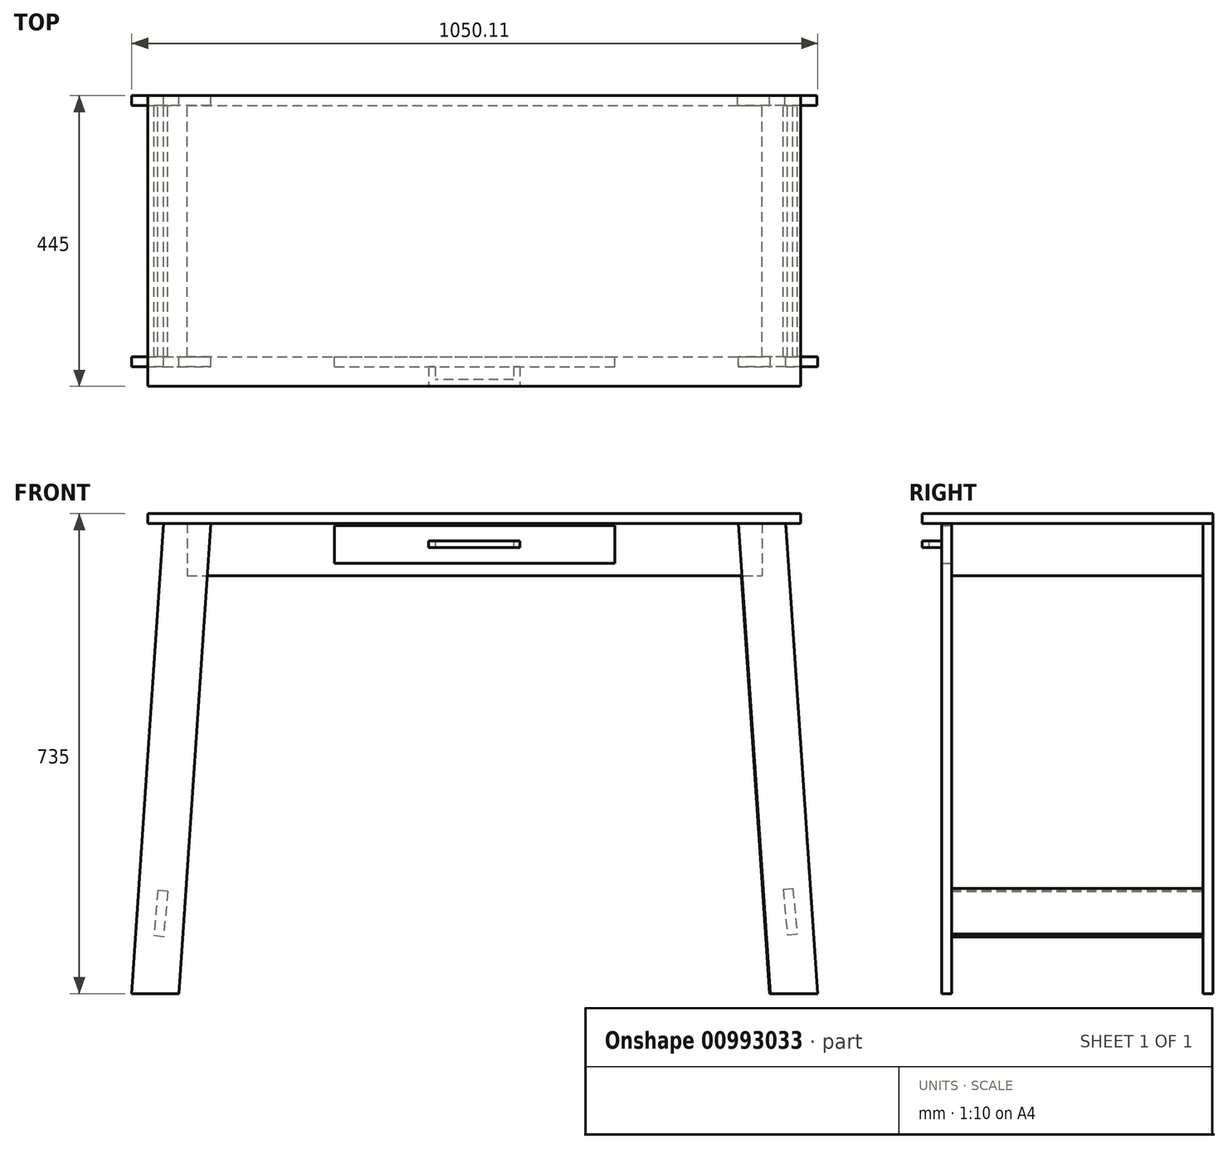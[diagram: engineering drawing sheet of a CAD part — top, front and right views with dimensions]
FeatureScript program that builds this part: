
annotation { "Feature Type Name" : "Feature", "Feature Type Description" : "" }
export const myFeature = defineFeature(function(context is Context, id is Id, definition is map)
    precondition{}
    {
        {
            var Q0;
            Q0=qCreatedBy(makeId("Front.planeOp"),FACE);
            var sketch = newSketch(context, id + "F0", { "sketchPlane" : qUnion([Q0])});
            skLineSegment(sketch, "E0.bottom", {"start": v(500, 7.5) * mm, "end": v(-500, 7.5) * mm});
            skLineSegment(sketch, "E0.top", {"start": v(500, -7.5) * mm, "end": v(-500, -7.5) * mm});
            skLineSegment(sketch, "E0.left", {"start": v(500, 7.5) * mm, "end": v(500, -7.5) * mm});
            skLineSegment(sketch, "E0.right", {"start": v(-500, 7.5) * mm, "end": v(-500, -7.5) * mm});
            skPoint(sketch, "E0.middle", {"position": v(0, 0) * mm});
            skLineSegment(sketch, "E1", {"start": v(-500, -7.5) * mm, "end": v(-475.48, -7.5) * mm});
            skLineSegment(sketch, "E2.bottom", {"start": v(-475.48, -7.5) * mm, "end": v(-403.32, -7.5) * mm});
            skLineSegment(sketch, "E2.left", {"start": v(-475.48, -7.5) * mm, "end": v(-524.46, -727.5) * mm});
            skLineSegment(sketch, "E2.right", {"start": v(-403.32, -7.5) * mm, "end": v(-452.29, -727.5) * mm});
            skLineSegment(sketch, "E3", {"start": v(-524.46, -727.5) * mm, "end": v(-452.29, -727.5) * mm});
            skLineSegment(sketch, "E4.MirrorCS", {"start": v(500, -7.5) * mm, "end": v(475.48, -7.5) * mm});
            skLineSegment(sketch, "E5.MirrorCS", {"start": v(475.48, -7.5) * mm, "end": v(403.32, -7.5) * mm});
            skLineSegment(sketch, "E6.MirrorCS", {"start": v(524.46, -727.5) * mm, "end": v(452.29, -727.5) * mm});
            skLineSegment(sketch, "E7.MirrorCS", {"start": v(475.48, -7.5) * mm, "end": v(524.46, -727.5) * mm});
            skLineSegment(sketch, "E8.MirrorCS", {"start": v(403.32, -7.5) * mm, "end": v(452.29, -727.5) * mm});
            skSolve(sketch);
        }
        {
            var Q0;
            Q0=makeQuery(id+"F0.imprint","IMPRINT",FACE,{"disambiguationData":[TD([[makeQuery(id+"F0.imprint","IMPRINT",EDGE,{"derivedFrom":sQuery(id+"F0.wireOp",EDGE,"E0.bottom")}),1.0]])]});
            extrude(context, id + "F1", {"entities" : qUnion([Q0]), "depth" : 445 * mm, "offsetDistance" : 25 * mm});
        }
        {
            var Q0;
            Q0=makeQuery(id+"F0.imprint","IMPRINT",FACE,{"disambiguationData":[TD([[makeQuery(id+"F0.imprint","IMPRINT",EDGE,{"derivedFrom":sQuery(id+"F0.wireOp",EDGE,"E2.left")}),1.0]])]});
            var Q1;
            Q1=makeQuery(id+"F0.imprint","IMPRINT",FACE,{"disambiguationData":[TD([[makeQuery(id+"F0.imprint","IMPRINT",EDGE,{"derivedFrom":sQuery(id+"F0.wireOp",EDGE,"E6.MirrorCS")}),-1.0]])]});
            extrude(context, id + "F2", {"entities" : qUnion([Q0, Q1]), "depth" : 15 * mm, "offsetDistance" : 25 * mm});
        }
        {
            var Q0;
            Q0=makeQuery(id+"F2.opExtrude","CAP_FACE",FACE,{"disambiguationData":[OSD([sQuery(id+"F0.wireOp",EDGE,"E2.left"),sQuery(id+"F0.wireOp",EDGE,"E2.right"),sQuery(id+"F0.wireOp",EDGE,"E2.bottom"),sQuery(id+"F0.wireOp",EDGE,"E3")])],"isStart":false});
            var sketch = newSketch(context, id + "F3", { "sketchPlane" : qUnion([Q0])});
            skLineSegment(sketch, "E9.bottom", {"start": v(-439.4, -7.5) * mm, "end": v(440.6, -7.5) * mm});
            skLineSegment(sketch, "E9.top", {"start": v(-439.4, -87.5) * mm, "end": v(440.6, -87.5) * mm});
            skLineSegment(sketch, "E9.left", {"start": v(-439.4, -7.5) * mm, "end": v(-439.4, -87.5) * mm});
            skLineSegment(sketch, "E9.right", {"start": v(440.6, -7.5) * mm, "end": v(440.6, -87.5) * mm});
            skLineSegment(sketch, "E10.bottom", {"start": v(-469.44, -570.71) * mm, "end": v(-484.38, -569.4) * mm});
            skLineSegment(sketch, "E10.top", {"start": v(-475.54, -640.45) * mm, "end": v(-490.48, -639.14) * mm});
            skLineSegment(sketch, "E10.left", {"start": v(-469.44, -570.71) * mm, "end": v(-475.54, -640.45) * mm});
            skLineSegment(sketch, "E10.right", {"start": v(-484.38, -569.4) * mm, "end": v(-490.48, -639.14) * mm});
            skPoint(sketch, "E11.endSnap0", {"position": v(0.6, -87.5) * mm});
            skLineSegment(sketch, "E12.MirrorCS", {"start": v(472.84, -567.9) * mm, "end": v(479.36, -637.6) * mm});
            skLineSegment(sketch, "E13.MirrorCS", {"start": v(487.78, -566.5) * mm, "end": v(494.3, -636.2) * mm});
            skLineSegment(sketch, "E14.MirrorCS", {"start": v(479.36, -637.6) * mm, "end": v(494.3, -636.2) * mm});
            skLineSegment(sketch, "E15.MirrorCS", {"start": v(472.84, -567.9) * mm, "end": v(487.78, -566.5) * mm});
            skSolve(sketch);
        }
        {
            var Q0;
            Q0 = qSketchRegion(id + "F3", true);
            extrude(context, id + "F4", {"entities" : qUnion([Q0]), "depth" : 385 * mm, "offsetDistance" : 25 * mm});
        }
        {
            var Q0;
            Q0=makeQuery(id+"F4.opExtrude","CAP_FACE",FACE,{"disambiguationData":[OSD([sQuery(id+"F3.wireOp",EDGE,"E9.bottom"),sQuery(id+"F3.wireOp",EDGE,"E9.top"),sQuery(id+"F3.wireOp",EDGE,"E9.left"),sQuery(id+"F3.wireOp",EDGE,"E9.right")])],"isStart":false});
            var sketch = newSketch(context, id + "F5", { "sketchPlane" : qUnion([Q0])});
            skLineSegment(sketch, "E16.bottom", {"start": v(-475.48, -7.5) * mm, "end": v(-403.32, -7.5) * mm});
            skLineSegment(sketch, "E16.left", {"start": v(-475.48, -7.5) * mm, "end": v(-524.46, -727.5) * mm});
            skLineSegment(sketch, "E16.right", {"start": v(-403.32, -7.5) * mm, "end": v(-452.29, -727.5) * mm});
            skLineSegment(sketch, "E17", {"start": v(-524.46, -727.5) * mm, "end": v(-452.29, -727.5) * mm});
            skLineSegment(sketch, "E18.MirrorCS", {"start": v(476.68, -7.5) * mm, "end": v(404.52, -7.5) * mm});
            skLineSegment(sketch, "E19.MirrorCS", {"start": v(525.65, -727.5) * mm, "end": v(453.49, -727.5) * mm});
            skLineSegment(sketch, "E20.MirrorCS", {"start": v(476.68, -7.5) * mm, "end": v(525.65, -727.5) * mm});
            skLineSegment(sketch, "E21.MirrorCS", {"start": v(404.52, -7.5) * mm, "end": v(453.49, -727.5) * mm});
            skPoint(sketch, "E22", {"position": v(440.6, -7.5) * mm});
            skPoint(sketch, "E23", {"position": v(-439.4, -7.5) * mm});
            skPoint(sketch, "E24.firstSnap0", {"position": v(0.6, -7.5) * mm});
            skLineSegment(sketch, "E24.bottom", {"start": v(0.6, -10.95) * mm, "end": v(-214.06, -10.95) * mm});
            skLineSegment(sketch, "E24.top", {"start": v(0.6, -68.47) * mm, "end": v(-214.06, -68.47) * mm});
            skLineSegment(sketch, "E24.right", {"start": v(-214.06, -10.95) * mm, "end": v(-214.06, -68.47) * mm});
            skLineSegment(sketch, "E25.MirrorCS", {"start": v(215.25, -10.95) * mm, "end": v(215.25, -68.47) * mm});
            skLineSegment(sketch, "E26.MirrorCS", {"start": v(0.6, -10.95) * mm, "end": v(215.25, -10.95) * mm});
            skLineSegment(sketch, "E27.MirrorCS", {"start": v(0.6, -68.47) * mm, "end": v(215.25, -68.47) * mm});
            skSolve(sketch);
        }
        {
            var Q0;
            Q0 = qSketchRegion(id + "F5", true);
            extrude(context, id + "F6", {"entities" : qUnion([Q0]), "depth" : 15 * mm, "offsetDistance" : 25 * mm});
        }
        {
            var Q0;
            Q0=makeQuery(id+"F6.opExtrude","CAP_FACE",FACE,{"disambiguationData":[OSD([sQuery(id+"F5.wireOp",EDGE,"E24.bottom"),sQuery(id+"F5.wireOp",EDGE,"E24.top"),sQuery(id+"F5.wireOp",EDGE,"E24.right"),sQuery(id+"F5.wireOp",EDGE,"E25.MirrorCS"),sQuery(id+"F5.wireOp",EDGE,"E26.MirrorCS"),sQuery(id+"F5.wireOp",EDGE,"E27.MirrorCS")])],"isStart":false});
            var sketch = newSketch(context, id + "F7", { "sketchPlane" : qUnion([Q0])});
            skLineSegment(sketch, "E28", {"start": v(0, 0) * mm, "end": v(0, -68.47) * mm});
            skLineSegment(sketch, "E29.bottom", {"start": v(-32.01, -34.28) * mm, "end": v(-42.01, -34.28) * mm});
            skLineSegment(sketch, "E29.top", {"start": v(-32.01, -44.28) * mm, "end": v(-42.01, -44.28) * mm});
            skLineSegment(sketch, "E29.left", {"start": v(-32.01, -34.28) * mm, "end": v(-32.01, -44.28) * mm});
            skLineSegment(sketch, "E29.right", {"start": v(-42.01, -34.28) * mm, "end": v(-42.01, -44.28) * mm});
            skPoint(sketch, "E29.middle", {"position": v(-37.01, -39.28) * mm});
            skLineSegment(sketch, "E30.MirrorCS", {"start": v(32.01, -34.28) * mm, "end": v(42.01, -34.28) * mm});
            skLineSegment(sketch, "E31.MirrorCS", {"start": v(32.01, -34.28) * mm, "end": v(32.01, -44.28) * mm});
            skLineSegment(sketch, "E32.MirrorCS", {"start": v(42.01, -34.28) * mm, "end": v(42.01, -44.28) * mm});
            skLineSegment(sketch, "E33.MirrorCS", {"start": v(32.01, -44.28) * mm, "end": v(42.01, -44.28) * mm});
            skPoint(sketch, "E34.MirrorP", {"position": v(37.01, -39.28) * mm});
            skSolve(sketch);
        }
        {
            var Q0;
            Q0 = qSketchRegion(id + "F7", true);
            extrude(context, id + "F8", {"entities" : qUnion([Q0]), "depth" : 20 * mm, "offsetDistance" : 25 * mm});
        }
        {
            var Q0;
            Q0=makeQuery(id+"F8.opExtrude","SWEPT_BODY",BODY,{"disambiguationData":[OSD([sQuery(id+"F7.wireOp",EDGE,"E29.bottom"),sQuery(id+"F7.wireOp",EDGE,"E29.top"),sQuery(id+"F7.wireOp",EDGE,"E29.left"),sQuery(id+"F7.wireOp",EDGE,"E29.right")])]});
            var Q1;
            Q1=makeQuery(id+"F8.opExtrude","SWEPT_BODY",BODY,{"disambiguationData":[OSD([sQuery(id+"F7.wireOp",EDGE,"E30.MirrorCS"),sQuery(id+"F7.wireOp",EDGE,"E31.MirrorCS"),sQuery(id+"F7.wireOp",EDGE,"E32.MirrorCS"),sQuery(id+"F7.wireOp",EDGE,"E33.MirrorCS")])]});
            deleteBodies(context, id + "F9", {"entities" : qUnion([Q0, Q1])});
        }
        {
            var Q0;
            Q0=makeQuery(id+"F6.opExtrude","CAP_FACE",FACE,{"disambiguationData":[OSD([sQuery(id+"F5.wireOp",EDGE,"E24.bottom"),sQuery(id+"F5.wireOp",EDGE,"E24.top"),sQuery(id+"F5.wireOp",EDGE,"E24.right"),sQuery(id+"F5.wireOp",EDGE,"E25.MirrorCS"),sQuery(id+"F5.wireOp",EDGE,"E26.MirrorCS"),sQuery(id+"F5.wireOp",EDGE,"E27.MirrorCS")])],"isStart":false});
            var sketch = newSketch(context, id + "F10", { "sketchPlane" : qUnion([Q0])});
            skLineSegment(sketch, "E35.bottom", {"start": v(-195.6, -53.4) * mm, "end": v(-154.7, -53.4) * mm});
            skLineSegment(sketch, "E35.top", {"start": v(-195.6, -25.27) * mm, "end": v(-154.7, -25.27) * mm});
            skLineSegment(sketch, "E35.left", {"start": v(-195.6, -53.4) * mm, "end": v(-195.6, -25.27) * mm});
            skLineSegment(sketch, "E35.right", {"start": v(-154.7, -53.4) * mm, "end": v(-154.7, -25.27) * mm});
            skSolve(sketch);
        }
        {
            var Q0;
            Q0 = qSketchRegion(id + "F10", true);
            extrude(context, id + "F11", {"entities" : qUnion([Q0]), "depth" : 30 * mm, "offsetDistance" : 25 * mm});
        }
        {
            var Q0;
            Q0=makeQuery(id+"F11.opExtrude","CAP_FACE",FACE,{"disambiguationData":[OSD([sQuery(id+"F10.wireOp",EDGE,"E35.bottom"),sQuery(id+"F10.wireOp",EDGE,"E35.top"),sQuery(id+"F10.wireOp",EDGE,"E35.left"),sQuery(id+"F10.wireOp",EDGE,"E35.right")])],"isStart":false});
            var sketch = newSketch(context, id + "F12", { "sketchPlane" : qUnion([Q0])});
            skPoint(sketch, "E36.startSnap0", {"position": v(-154.7, -39.33) * mm});
            skLineSegment(sketch, "E37.bottom", {"start": v(70, -34.33) * mm, "end": v(-70, -34.33) * mm});
            skLineSegment(sketch, "E37.top", {"start": v(70, -44.33) * mm, "end": v(-70, -44.33) * mm});
            skLineSegment(sketch, "E37.left", {"start": v(70, -34.33) * mm, "end": v(70, -44.33) * mm});
            skLineSegment(sketch, "E37.right", {"start": v(-70, -34.33) * mm, "end": v(-70, -44.33) * mm});
            skPoint(sketch, "E37.middle", {"position": v(0, -39.33) * mm});
            skSolve(sketch);
        }
        {
            var Q0;
            Q0 = qSketchRegion(id + "F12", true);
            extrude(context, id + "F13", {"entities" : qUnion([Q0]), "oppositeDirection" : true, "depth" : 10 * mm, "offsetDistance" : 25 * mm});
        }
        {
            var Q0;
            Q0=makeQuery(id+"F11.opExtrude","SWEPT_BODY",BODY,{"disambiguationData":[OSD([sQuery(id+"F10.wireOp",EDGE,"E35.bottom"),sQuery(id+"F10.wireOp",EDGE,"E35.top"),sQuery(id+"F10.wireOp",EDGE,"E35.left"),sQuery(id+"F10.wireOp",EDGE,"E35.right")])]});
            deleteBodies(context, id + "F14", {"entities" : qUnion([Q0])});
        }
        {
            var Q0;
            Q0=makeQuery(id+"F13.opExtrude","CAP_FACE",FACE,{"disambiguationData":[OSD([sQuery(id+"F12.wireOp",EDGE,"E37.bottom"),sQuery(id+"F12.wireOp",EDGE,"E37.top"),sQuery(id+"F12.wireOp",EDGE,"E37.left"),sQuery(id+"F12.wireOp",EDGE,"E37.right")])],"isStart":false});
            var sketch = newSketch(context, id + "F15", { "sketchPlane" : qUnion([Q0])});
            skLineSegment(sketch, "E38.bottom", {"start": v(-70, -34.33) * mm, "end": v(-60, -34.33) * mm});
            skLineSegment(sketch, "E38.top", {"start": v(-70, -44.33) * mm, "end": v(-60, -44.33) * mm});
            skLineSegment(sketch, "E38.left", {"start": v(-70, -34.33) * mm, "end": v(-70, -44.33) * mm});
            skLineSegment(sketch, "E38.right", {"start": v(-60, -34.33) * mm, "end": v(-60, -44.33) * mm});
            skLineSegment(sketch, "E39.bottom", {"start": v(70, -34.33) * mm, "end": v(60, -34.33) * mm});
            skLineSegment(sketch, "E39.top", {"start": v(70, -44.33) * mm, "end": v(60, -44.33) * mm});
            skLineSegment(sketch, "E39.left", {"start": v(70, -34.33) * mm, "end": v(70, -44.33) * mm});
            skLineSegment(sketch, "E39.right", {"start": v(60, -34.33) * mm, "end": v(60, -44.33) * mm});
            skSolve(sketch);
        }
        {
            var Q0;
            Q0 = qSketchRegion(id + "F15", true);
            extrude(context, id + "F16", {"entities" : qUnion([Q0]), "operationType" : NewBodyOperationType.ADD, "depth" : 20 * mm, "offsetDistance" : 25 * mm});
        }
    });
